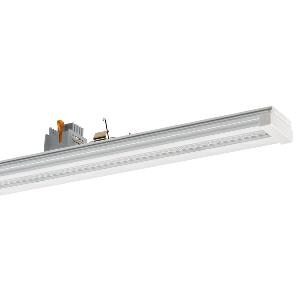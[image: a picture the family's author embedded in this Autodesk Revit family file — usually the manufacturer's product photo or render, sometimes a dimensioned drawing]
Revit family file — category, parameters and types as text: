
# Revit family: conveo_-_cvg_8000_850_w-l_da_7_226848289-00804967_df58
name_source: partatom
category: Lighting Fixtures
units: mm (PartAtom-declared; Revit-internal decimal feet)

## family parameters
Cut with Voids When Loaded = No
Host = Face
Light Source = No
Part Type = Normal
Room Calculation Point = No
Round Connector Dimension = Use Diameter
Shared = No

## types (1)
- CONVEO - CVG 8000/850/W-L/DA/7 (1 x LED, 8100 lm, 5000K)
    Apparent Load = 47 VA
    Approval mark = CE
    CIE Flux Codes = 85 97 99 100 100
    Color Rendering = 80-89
    Color Temperature = 5000K
    Control Gear = Electronic ballast
    Default Elevation = 1800 mm
    Description = CVG 8000/850/W-L/DA/7|Continuous-row system|light source: LED|work equipment: Adjustable electronic ballast, digital DALI|connected load: 220-240 V, 50-60 Hz|Power consumption: approx. 47 W|luminous flux: 8100 lm|luminous efficacy: 172 lm/W|colour temperature: Cold white, ca. 5000 K|color rendering index (CRI): >= 80|chromaticity tolerance:  3 SDCM|System of protection: IP 54|class of protection: I|technology: Continuously dimmable|luminaire body|material: Aluminium|surface: Powder coatet|colour: White|lamp cover: Acrylic (PMMA), Satine|weight (net): approx. 1.9 kg|Fastening: Available separately|maximum ambient temperature: 42 ░C|glare control: Lens optics|Approval mark: VDE - ENEC|
    Frequency = 50 Hz
    Height = 70 mm
    Lamp = 1 x LED
    Lamp Light Flux = 8100 lm
    Lamp count = 1
    Length = 1500 mm
    Luminous efficacy = 172 lm/W
    Manufacturer = Waldmann
    ModVariant = No
    Model = 226848289-00804967
    Mounting Place = Ceiling
    Mounting Type = Pendant
    Number of Poles = 1
    OnlyDefault = Yes
    Power Factor = 1
    Product Name = CONVEO - CVG 8000/850/W-L/DA/7
    Product group = Continuous-row system (industry)
    ProductGroupID = 301
    Protection Class = Protection class I
    Protection Degree = IP 54
    RLX_Detail_Level = 1
    RlxData = <blob elided: 99537 chars, md5=31e38185>
    Socket = socket
    Standby Power = 0 W
    System Light Flux = 8100 lm
    System Power = 47 W
    Type Comments = Product without accessories
    Type Image = 226848259-00804964_1l7.jpg
    URL = http://relux.com
    VarID = ---
    Voltage = 230 V
    Voltage Range = 220-240 V
    Weight = 0.00 kg
    Width = 64 mm

## geometry (parser evidence)
native form markers: Blend x4, Sweep x9
no freeform markers — native parametric forms only
